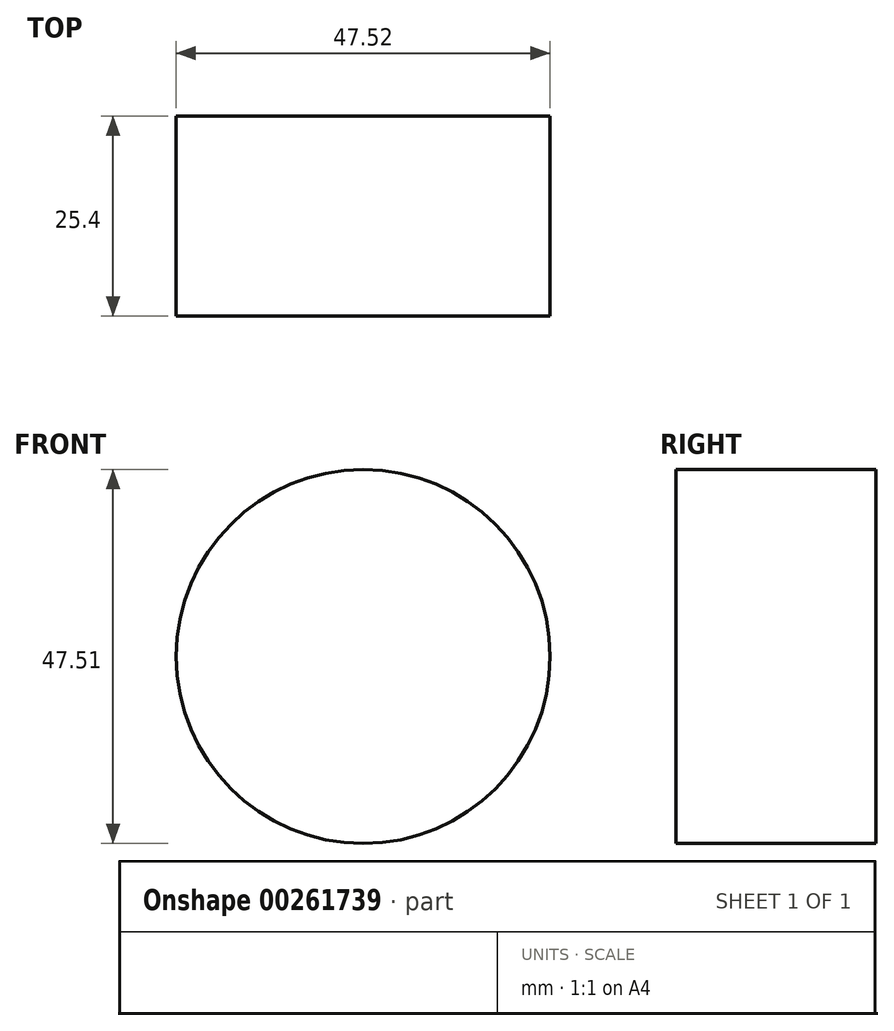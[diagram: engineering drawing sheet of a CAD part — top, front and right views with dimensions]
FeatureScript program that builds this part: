
annotation { "Feature Type Name" : "Feature", "Feature Type Description" : "" }
export const myFeature = defineFeature(function(context is Context, id is Id, definition is map)
    precondition{}
    {
        {
            var Q0;
            Q0=qCreatedBy(makeId("Front.planeOp"),FACE);
            var sketch = newSketch(context, id + "F0", { "sketchPlane" : qUnion([Q0])});
            skLineSegment(sketch, "E0.bottom", {"start": v(49.76, -8.43) * mm, "end": v(92.05, -8.43) * mm});
            skLineSegment(sketch, "E0.top", {"start": v(49.76, 61.39) * mm, "end": v(92.05, 61.39) * mm});
            skLineSegment(sketch, "E0.left", {"start": v(49.76, -8.43) * mm, "end": v(49.76, 61.39) * mm});
            skLineSegment(sketch, "E0.right", {"start": v(92.05, -8.43) * mm, "end": v(92.05, 61.39) * mm});
            skCircle(sketch, "E1", {"center": v(111.46, -41.92) * mm, "radius": 23.76 * mm});
            skSolve(sketch);
        }
        {
            var Q0;
            Q0=makeQuery(id+"F0.imprint","IMPRINT",FACE,{"disambiguationData":[TD([[makeQuery(id+"F0.imprint","IMPRINT",EDGE,{"derivedFrom":sQuery(id+"F0.wireOp",EDGE,"E1")}),1.0]])]});
            extrude(context, id + "F1", {"entities" : qUnion([Q0]), "depth" : 25.4 * mm});
        }
    });
